# Revit family: LBMS3W_DOWNLIGHT MINIS
name_source: partatom
category: Luminarias
units: mm (PartAtom-declared; Revit-internal decimal feet)

## family parameters
Compartido = No
Corte con vacíos al cargar = No
Cota de conector redondo = Diámetro de uso
Origen de luz = Sí
Punto de cálculo de habitación = No
Se basa en plano de trabajo = Sí
Siempre vertical = Sí
Tipo de pieza = Normal

## types (1)
- DOWNLIGHT MINI S_LBMS3W
    Cambio de temperatura de color de luz atenuada = <Ninguno>
    Comentarios de vataje = 12V
    Descripción = LUMINARIA MINI, TIPO CIRCULAR, PARA EMPOTRAR EN TECHO CON 35MM DE DIAMETRO POR 24MM DE HOUSING, CUERPO Y ANILLO EN COLOR NEGRO, IP 20 USO PARA INTERIORES, CUENTA CON 1 LED TIPO OSRAM CON UNA POTENCIA DE 2.2W, A UNA TEMPERATURA EN BLANCO CALIDO 3000K, IRC 80, APERTURA A 40 GRADOS, ALIMENTADA A 12V. REQUIERE ACCESORIOS.
    Elevación por defecto = 1219 mm
    Fabricante = BRILLANT
    Filtro de color = 16777215
    Longitud de símbolo de origen de luz = 500 mm  [stored 1.64042 ft]
    Lámpara = Osram
    Modelo = LBMS3W
    Radio ext = 18 mm
    Radio int = 13 mm
    Watt per fixture = 2.2
    Ángulo de campo de foco = 40.00°
    Ángulo de enfoque = 40.00°
    Ángulo de inclinación = 60.00°

note: [stored X ft] marks values corroborated as IEEE doubles in the binary element streams (Revit-internal decimal feet)

## geometry (parser evidence)
native form markers: Blend x2
no freeform markers — native parametric forms only
